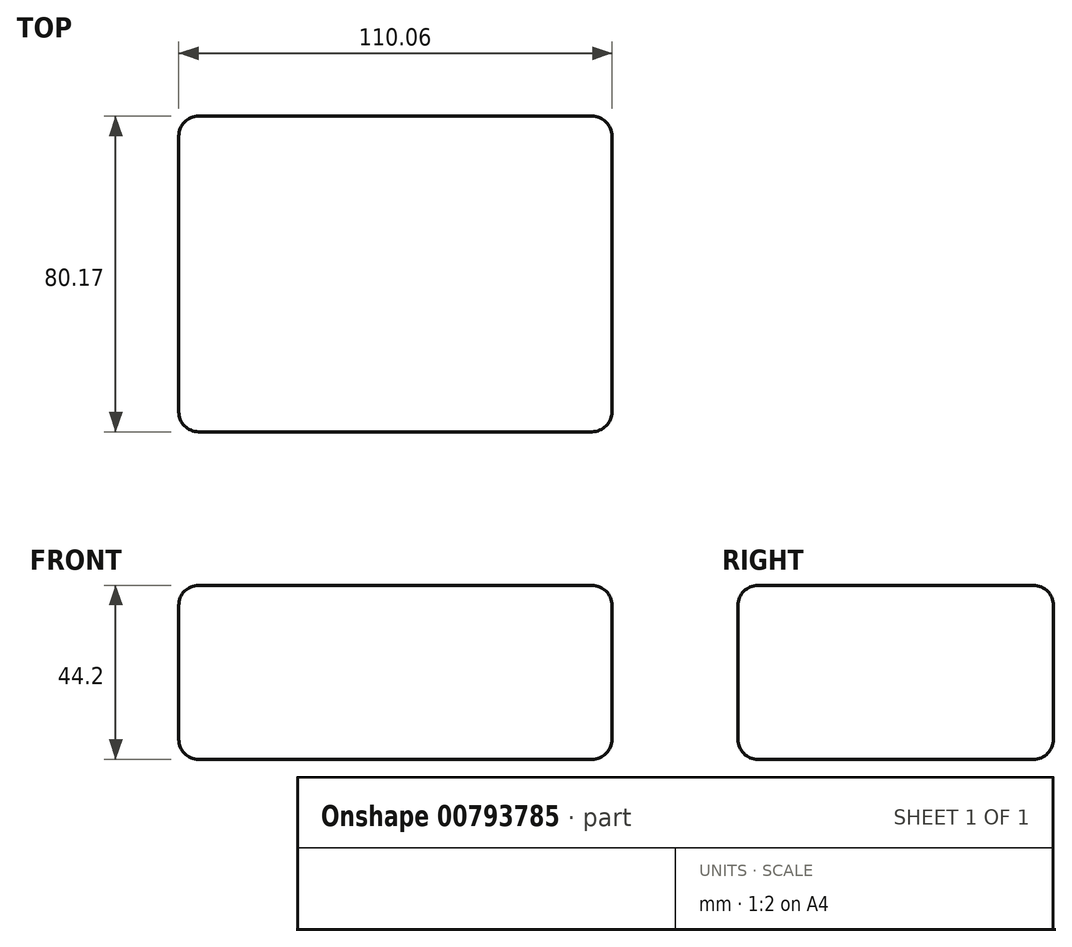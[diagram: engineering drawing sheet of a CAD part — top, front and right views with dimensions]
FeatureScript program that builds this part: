
annotation { "Feature Type Name" : "Feature", "Feature Type Description" : "" }
export const myFeature = defineFeature(function(context is Context, id is Id, definition is map)
    precondition{}
    {
        {
            var Q0;
            Q0=qCreatedBy(makeId("Top.planeOp"),FACE);
            var sketch = newSketch(context, id + "F0", { "sketchPlane" : qUnion([Q0])});
            skLineSegment(sketch, "E0.bottom", {"start": v(-51.16, 34.86) * mm, "end": v(58.9, 34.86) * mm});
            skLineSegment(sketch, "E0.top", {"start": v(-51.16, -45.3) * mm, "end": v(58.9, -45.3) * mm});
            skLineSegment(sketch, "E0.left", {"start": v(-51.16, 34.86) * mm, "end": v(-51.16, -45.3) * mm});
            skLineSegment(sketch, "E0.right", {"start": v(58.9, 34.86) * mm, "end": v(58.9, -45.3) * mm});
            skSolve(sketch);
        }
        {
            var Q0;
            Q0 = qSketchRegion(id + "F0", true);
            extrude(context, id + "F1", {"entities" : qUnion([Q0]), "depth" : 44.2 * mm, "offsetDistance" : 25.4 * mm});
        }
        {
            var Q0;
            Q0=makeQuery(id+"F1.opExtrude","CAP_EDGE",EDGE,{"disambiguationData":[OSD([sQuery(id+"F0.wireOp",EDGE,"E0.left")])],"isStart":false});
            var Q1;
            Q1=makeQuery(id+"F1.opExtrude","CAP_EDGE",EDGE,{"disambiguationData":[OSD([sQuery(id+"F0.wireOp",EDGE,"E0.top")])],"isStart":false});
            var Q2;
            Q2=makeQuery(id+"F1.opExtrude","CAP_EDGE",EDGE,{"disambiguationData":[OSD([sQuery(id+"F0.wireOp",EDGE,"E0.right")])],"isStart":false});
            var Q3;
            Q3=makeQuery(id+"F1.opExtrude","CAP_EDGE",EDGE,{"disambiguationData":[OSD([sQuery(id+"F0.wireOp",EDGE,"E0.bottom")])],"isStart":false});
            var Q4;
            Q4=makeQuery(id+"F1.opExtrude","SWEPT_EDGE",EDGE,{"disambiguationData":[OSD([sQuery(id+"F0.wireOp",EDGE,"E0.top"),sQuery(id+"F0.wireOp",EDGE,"E0.right")])]});
            var Q5;
            Q5=makeQuery(id+"F1.opExtrude","SWEPT_EDGE",EDGE,{"disambiguationData":[OSD([sQuery(id+"F0.wireOp",EDGE,"E0.top"),sQuery(id+"F0.wireOp",EDGE,"E0.left")])]});
            var Q6;
            Q6=makeQuery(id+"F1.opExtrude","CAP_EDGE",EDGE,{"disambiguationData":[OSD([sQuery(id+"F0.wireOp",EDGE,"E0.top")])],"isStart":true});
            var Q7;
            Q7=makeQuery(id+"F1.opExtrude","CAP_EDGE",EDGE,{"disambiguationData":[OSD([sQuery(id+"F0.wireOp",EDGE,"E0.right")])],"isStart":true});
            var Q8;
            Q8=makeQuery(id+"F1.opExtrude","SWEPT_EDGE",EDGE,{"disambiguationData":[OSD([sQuery(id+"F0.wireOp",EDGE,"E0.bottom"),sQuery(id+"F0.wireOp",EDGE,"E0.right")])]});
            var Q9;
            Q9=makeQuery(id+"F1.opExtrude","CAP_EDGE",EDGE,{"disambiguationData":[OSD([sQuery(id+"F0.wireOp",EDGE,"E0.bottom")])],"isStart":true});
            var Q10;
            Q10=makeQuery(id+"F1.opExtrude","CAP_EDGE",EDGE,{"disambiguationData":[OSD([sQuery(id+"F0.wireOp",EDGE,"E0.left")])],"isStart":true});
            var Q11;
            Q11=makeQuery(id+"F1.opExtrude","SWEPT_EDGE",EDGE,{"disambiguationData":[OSD([sQuery(id+"F0.wireOp",EDGE,"E0.bottom"),sQuery(id+"F0.wireOp",EDGE,"E0.left")])]});
            fillet(context, id + "F2", {"entities" : qUnion([Q0, Q1, Q2, Q3, Q4, Q5, Q6, Q7, Q8, Q9, Q10, Q11]), "radius" : 5.08 * mm, "tangentPropagation" : true, "allowEdgeOverflow" : false});
        }
    });
